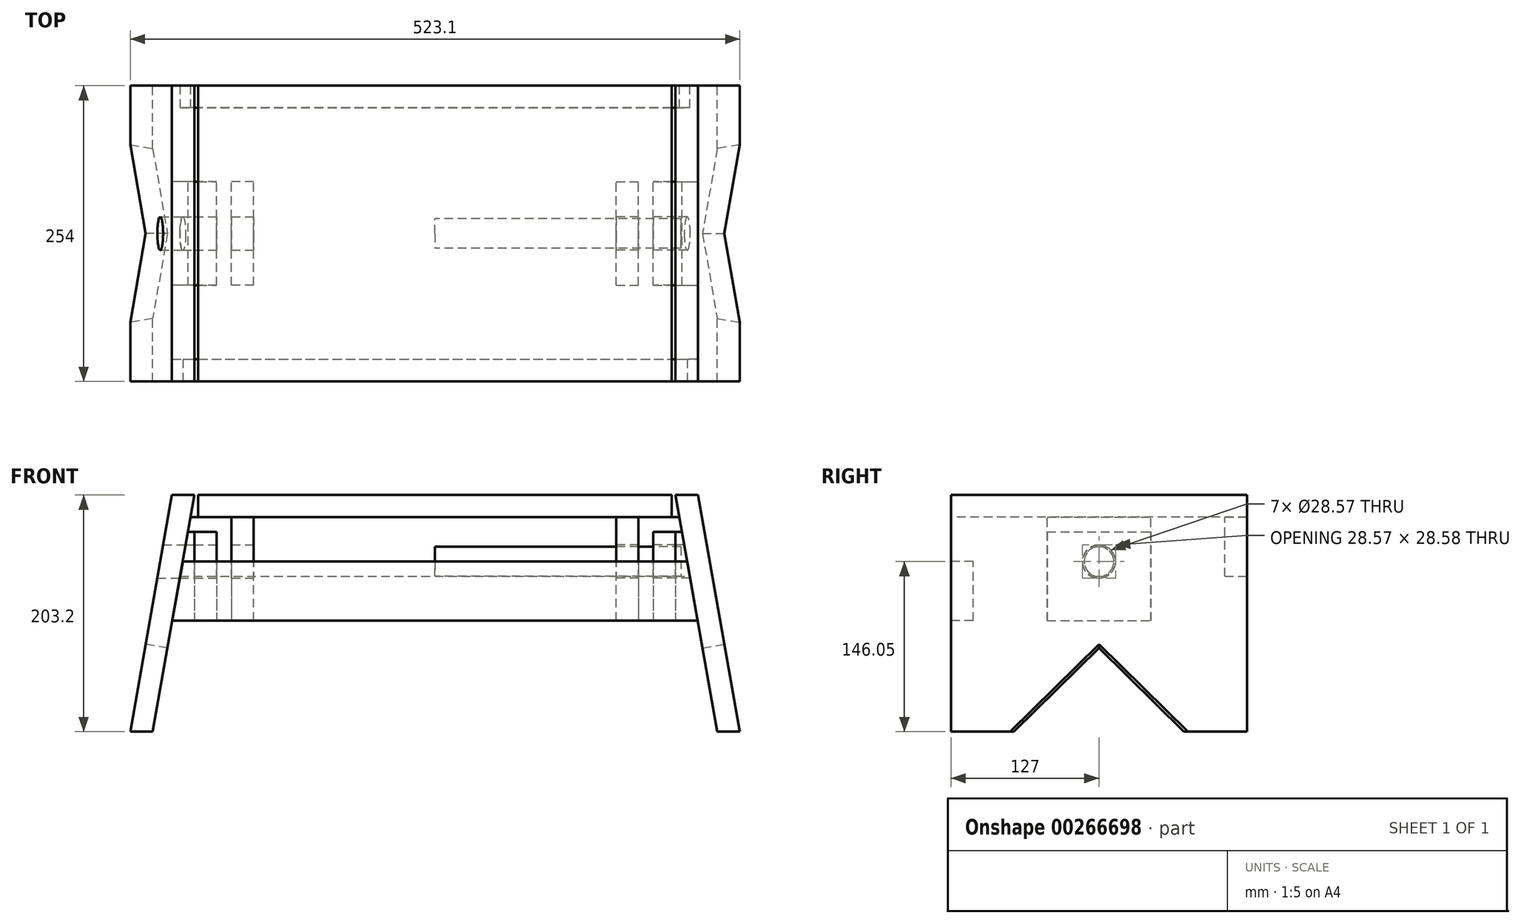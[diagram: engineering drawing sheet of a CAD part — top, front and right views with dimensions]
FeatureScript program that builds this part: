
annotation { "Feature Type Name" : "Feature", "Feature Type Description" : "" }
export const myFeature = defineFeature(function(context is Context, id is Id, definition is map)
    precondition{}
    {
        {
            var Q0;
            Q0=qCreatedBy(makeId("Top.planeOp"),FACE);
            var sketch = newSketch(context, id + "F0", { "sketchPlane" : qUnion([Q0])});
            skLineSegment(sketch, "E0.bottom", {"start": v(-203.2, 127) * mm, "end": v(203.2, 127) * mm});
            skLineSegment(sketch, "E0.top", {"start": v(-203.2, -127) * mm, "end": v(203.2, -127) * mm});
            skLineSegment(sketch, "E0.left", {"start": v(-203.2, 127) * mm, "end": v(-203.2, -127) * mm});
            skLineSegment(sketch, "E0.right", {"start": v(203.2, 127) * mm, "end": v(203.2, -127) * mm});
            skPoint(sketch, "E0.middle", {"position": v(0, 0) * mm});
            skSolve(sketch);
        }
        {
            var Q0;
            Q0 = qSketchRegion(id + "F0", true);
            extrude(context, id + "F1", {"entities" : qUnion([Q0]), "depth" : 19.05 * mm});
        }
        {
            var Q0;
            Q0=qCreatedBy(makeId("Front.planeOp"),FACE);
            var sketch = newSketch(context, id + "F2", { "sketchPlane" : qUnion([Q0])});
            skLineSegment(sketch, "E1", {"start": v(225.72, 19.05) * mm, "end": v(206.38, 19.05) * mm});
            skLineSegment(sketch, "E2", {"start": v(206.38, 19.05) * mm, "end": v(242.2, -184.15) * mm});
            skLineSegment(sketch, "E3", {"start": v(242.2, -184.15) * mm, "end": v(261.55, -184.15) * mm});
            skLineSegment(sketch, "E4", {"start": v(261.55, -184.15) * mm, "end": v(225.72, 19.05) * mm});
            skSolve(sketch);
        }
        {
            var Q0;
            Q0 = qSketchRegion(id + "F2", true);
            var Q1;
            Q1=makeQuery(id+"F1.opExtrude","SWEPT_FACE",FACE,{"disambiguationData":[OSD([sQuery(id+"F0.wireOp",EDGE,"E0.top")])]});
            var Q2;
            Q2=makeQuery(id+"F1.opExtrude","SWEPT_FACE",FACE,{"disambiguationData":[OSD([sQuery(id+"F0.wireOp",EDGE,"E0.bottom")])]});
            extrude(context, id + "F3", {"entities" : qUnion([Q0]), "endBound" : BoundingType.UP_TO_SURFACE, "endBoundEntityFace" : qUnion([Q1]), "depth" : 25.4 * mm, "hasSecondDirection" : true, "secondDirectionBound" : SecondDirectionBoundingType.UP_TO_SURFACE, "secondDirectionOppositeDirection" : true, "secondDirectionBoundEntityFace" : qUnion([Q2]), "secondDirectionDepth" : 25.4 * mm});
        }
        {
            var Q0;
            Q0=makeQuery(id+"F3.opExtrude","SWEPT_FACE",FACE,{"disambiguationData":[OSD([sQuery(id+"F2.wireOp",EDGE,"E4")])]});
            var sketch = newSketch(context, id + "F4", { "sketchPlane" : qUnion([Q0])});
            skLineSegment(sketch, "E5", {"start": v(-76.2, -226.77) * mm, "end": v(0, -150.57) * mm});
            skLineSegment(sketch, "E6", {"start": v(0, -150.57) * mm, "end": v(76.2, -226.77) * mm});
            skLineSegment(sketch, "E7", {"start": v(76.2, -226.77) * mm, "end": v(-76.2, -226.77) * mm});
            skSolve(sketch);
        }
        {
            var Q0;
            Q0 = qSketchRegion(id + "F4", true);
            extrude(context, id + "F5", {"entities" : qUnion([Q0]), "operationType" : NewBodyOperationType.REMOVE, "endBound" : BoundingType.UP_TO_NEXT, "oppositeDirection" : true, "depth" : 25.4 * mm});
        }
        {
            var Q0;
            Q0=makeQuery(id+"F3.opExtrude","SWEPT_BODY",BODY,{"disambiguationData":[OSD([sQuery(id+"F2.wireOp",EDGE,"E1"),sQuery(id+"F2.wireOp",EDGE,"E2"),sQuery(id+"F2.wireOp",EDGE,"E3"),sQuery(id+"F2.wireOp",EDGE,"E4")])]});
            var Q1;
            Q1=qCreatedBy(makeId("Right.planeOp"),FACE);
            mirror(context, id + "F6", {"entities" : qUnion([Q0]), "mirrorPlane" : qUnion([Q1])});
        }
        {
            var Q0;
            Q0=makeQuery(id+"F1.opExtrude","SWEPT_FACE",FACE,{"disambiguationData":[OSD([sQuery(id+"F0.wireOp",EDGE,"E0.top")])]});
            var sketch = newSketch(context, id + "F7", { "sketchPlane" : qUnion([Q0])});
            skLineSegment(sketch, "E8.0", {"start": v(-225.4, -88.9) * mm, "end": v(-216.45, -38.1) * mm});
            skLineSegment(sketch, "E9.0", {"start": v(225.4, -88.9) * mm, "end": v(216.45, -38.1) * mm});
            skLineSegment(sketch, "E10", {"start": v(-225.4, -88.9) * mm, "end": v(225.4, -88.9) * mm});
            skPoint(sketch, "E11.orphan", {"position": v(-242.2, -184.15) * mm});
            skPoint(sketch, "E12.orphan", {"position": v(242.2, -184.15) * mm});
            skLineSegment(sketch, "E13", {"start": v(-216.45, -38.1) * mm, "end": v(216.45, -38.1) * mm});
            skSolve(sketch);
        }
        {
            var Q0;
            Q0 = qSketchRegion(id + "F7", true);
            extrude(context, id + "F8", {"entities" : qUnion([Q0]), "oppositeDirection" : true, "depth" : 19.05 * mm});
        }
        {
            var Q0;
            Q0=qCreatedBy(makeId("Front.planeOp"),FACE);
            var sketch = newSketch(context, id + "F9", { "sketchPlane" : qUnion([Q0])});
            skLineSegment(sketch, "E14.bottom", {"start": v(-211.04, -25.4) * mm, "end": v(211.04, -25.4) * mm});
            skLineSegment(sketch, "E14.top", {"start": v(-211.04, -50.8) * mm, "end": v(211.04, -50.8) * mm});
            skLineSegment(sketch, "E14.left", {"start": v(-211.04, -25.4) * mm, "end": v(-211.04, -50.8) * mm});
            skLineSegment(sketch, "E14.right", {"start": v(211.04, -25.4) * mm, "end": v(211.04, -50.8) * mm});
            skLineSegment(sketch, "E15", {"start": v(-211.04, -25.4) * mm, "end": v(-214.21, -25.4) * mm, "construction": true});
            skLineSegment(sketch, "E16", {"start": v(-211.04, -38.1) * mm, "end": v(211.04, -38.1) * mm});
            skLineSegment(sketch, "E17", {"start": v(-206.36, -12.7) * mm, "end": v(-206.36, -88.9) * mm});
            skLineSegment(sketch, "E18", {"start": v(-206.36, -88.9) * mm, "end": v(-225.4, -88.9) * mm});
            skLineSegment(sketch, "E19", {"start": v(-206.36, -12.7) * mm, "end": v(-211.97, -12.7) * mm});
            skLineSegment(sketch, "E20", {"start": v(-211.97, -12.7) * mm, "end": v(-225.4, -88.9) * mm});
            skLineSegment(sketch, "E21", {"start": v(-174.6, 0) * mm, "end": v(-174.6, -88.9) * mm});
            skLineSegment(sketch, "E22", {"start": v(-174.6, -88.9) * mm, "end": v(-155.56, -88.9) * mm});
            skLineSegment(sketch, "E23", {"start": v(-155.56, -88.9) * mm, "end": v(-155.56, 0) * mm});
            skLineSegment(sketch, "E24", {"start": v(-155.56, 0) * mm, "end": v(-174.6, 0) * mm});
            skLineSegment(sketch, "E25", {"start": v(-174.6, -23.81) * mm, "end": v(-155.56, -23.81) * mm});
            skLineSegment(sketch, "E26", {"start": v(-174.6, -52.39) * mm, "end": v(-155.56, -52.39) * mm});
            skLineSegment(sketch, "E27", {"start": v(-206.36, -12.7) * mm, "end": v(-187.3, -12.7) * mm});
            skLineSegment(sketch, "E28", {"start": v(-187.3, -12.7) * mm, "end": v(-187.3, -88.9) * mm});
            skLineSegment(sketch, "E29", {"start": v(-187.3, -88.9) * mm, "end": v(-206.36, -88.9) * mm});
            skSolve(sketch);
        }
        {
            var Q0;
            Q0=qCreatedBy(makeId("Right.planeOp"),FACE);
            var sketch = newSketch(context, id + "F10", { "sketchPlane" : qUnion([Q0])});
            skCircle(sketch, "E30", {"center": v(0, -38.1) * mm, "radius": 12.7 * mm});
            skLineSegment(sketch, "E31", {"start": v(0, -38.1) * mm, "end": v(-17.15, 16.42) * mm, "construction": true});
            skLineSegment(sketch, "E32", {"start": v(-138.3, -21.68) * mm, "end": v(104, 54.52) * mm, "construction": true});
            skLineSegment(sketch, "E33", {"start": v(0, -38.1) * mm, "end": v(0, 19.05) * mm, "construction": true});
            skLineSegment(sketch, "E34", {"start": v(-138.3, -21.68) * mm, "end": v(-132.58, -39.85) * mm, "construction": true});
            skLineSegment(sketch, "E35", {"start": v(-132.58, -39.85) * mm, "end": v(109.72, 36.35) * mm, "construction": true});
            skLineSegment(sketch, "E36", {"start": v(109.72, 36.35) * mm, "end": v(104, 54.52) * mm, "construction": true});
            skCircle(sketch, "E37", {"center": v(0, -38.1) * mm, "radius": 14.29 * mm});
            skPoint(sketch, "E38.0", {"position": v(0, -25.4) * mm});
            skPoint(sketch, "E39.0", {"position": v(0, -23.81) * mm});
            skSolve(sketch);
        }
        {
            var Q0;
            {var subQ0=sQuery(id+"F9.wireOp",EDGE,"E19");Q0=makeQuery(id+"F9.imprint","IMPRINT",FACE,{"disambiguationData":[TD([[makeQuery(id+"F9.imprint","IMPRINT",EDGE,{"derivedFrom":subQ0}),1.0]])]});}
            var Q1;
            {var subQ0=sQuery(id+"F9.wireOp",EDGE,"E18");Q1=makeQuery(id+"F9.imprint","IMPRINT",FACE,{"disambiguationData":[TD([[makeQuery(id+"F9.imprint","IMPRINT",EDGE,{"derivedFrom":subQ0}),-1.0]])]});}
            var Q2;
            {var subQ5=sQuery(id+"F9.wireOp",EDGE,"QS01VHn4-kFqK-0E2x-3ZNE-qvUShlXBOCAW");Q2=makeQuery(id+"F9.imprint","IMPRINT",FACE,{"disambiguationData":[TD([[makeQuery(id+"F9.imprint","IMPRINT",EDGE,{"derivedFrom":subQ5}),1.0]])]});}
            var Q3;
            {var subQ0=sQuery(id+"F9.wireOp",EDGE,"E14.left");var subQ1=sQuery(id+"F9.wireOp",EDGE,"E14.bottom");var subQ2=makeQuery(id+"F9.imprint","INTERSECT",VERTEX,{"derivedFrom":[subQ1,subQ0]});Q3=makeQuery(id+"F9.imprint","IMPRINT",FACE,{"disambiguationData":[TD([[makeQuery(id+"F9.imprint","IMPRINT",EDGE,{"disambiguationData":[TD([[subQ2,-1.0]])],"derivedFrom":subQ1}),-1.0]])]});}
            var Q4;
            {var subQ0=sQuery(id+"F9.wireOp",EDGE,"E14.left");var subQ1=sQuery(id+"F9.wireOp",EDGE,"E14.top");var subQ2=makeQuery(id+"F9.imprint","INTERSECT",VERTEX,{"derivedFrom":[subQ1,subQ0]});Q4=makeQuery(id+"F9.imprint","IMPRINT",FACE,{"disambiguationData":[TD([[makeQuery(id+"F9.imprint","IMPRINT",EDGE,{"disambiguationData":[TD([[subQ2,-1.0]])],"derivedFrom":subQ1}),1.0]])]});}
            var Q5;
            Q5=sQuery(id+"F9.wireOp",EDGE,"E17");
            var Q6;
            Q6=sQuery(id+"F9.wireOp",EDGE,"E18");
            var Q7;
            Q7=sQuery(id+"F9.wireOp",EDGE,"E20");
            var Q8;
            Q8=sQuery(id+"F9.wireOp",EDGE,"E19");
            extrude(context, id + "F11", {"entities" : qUnion([Q0, Q1, Q2, Q3, Q4]), "surfaceEntities" : qUnion([Q5, Q6, Q7, Q8]), "endBound" : BoundingType.SYMMETRIC, "depth" : 88.9 * mm});
        }
        {
            var Q0;
            Q0=makeQuery(id+"F10.imprint","IMPRINT",FACE,{"disambiguationData":[TD([[makeQuery(id+"F10.imprint","IMPRINT",EDGE,{"derivedFrom":sQuery(id+"F10.wireOp",EDGE,"E30")}),-1.0]])]});
            var Q1;
            Q1=makeQuery(id+"F10.imprint","IMPRINT",FACE,{"disambiguationData":[TD([[makeQuery(id+"F10.imprint","IMPRINT",EDGE,{"derivedFrom":sQuery(id+"F10.wireOp",EDGE,"E30")}),1.0]])]});
            extrude(context, id + "F12", {"entities" : qUnion([Q0, Q1]), "operationType" : NewBodyOperationType.REMOVE, "endBound" : BoundingType.THROUGH_ALL, "oppositeDirection" : true, "depth" : 25.4 * mm});
        }
        {
            var Q0;
            {var subQ0=sQuery(id+"F9.wireOp",EDGE,"E14.right");var subQ1=sQuery(id+"F9.wireOp",EDGE,"E14.top");var subQ2=makeQuery(id+"F9.imprint","INTERSECT",VERTEX,{"derivedFrom":[subQ1,subQ0]});Q0=makeQuery(id+"F9.imprint","IMPRINT",FACE,{"disambiguationData":[TD([[makeQuery(id+"F9.imprint","IMPRINT",EDGE,{"disambiguationData":[TD([[subQ2,1.0]])],"derivedFrom":subQ1}),1.0]])]});}
            var Q1;
            {var subQ0=sQuery(id+"F9.wireOp",EDGE,"E14.left");var subQ1=sQuery(id+"F9.wireOp",EDGE,"E14.top");var subQ2=makeQuery(id+"F9.imprint","INTERSECT",VERTEX,{"derivedFrom":[subQ1,subQ0]});Q1=makeQuery(id+"F9.imprint","IMPRINT",FACE,{"disambiguationData":[TD([[makeQuery(id+"F9.imprint","IMPRINT",EDGE,{"disambiguationData":[TD([[subQ2,-1.0]])],"derivedFrom":subQ1}),1.0]])]});}
            var Q2;
            {var subQ0=sQuery(id+"F9.wireOp",EDGE,"E21");var subQ1=sQuery(id+"F9.wireOp",EDGE,"E14.top");var subQ2=makeQuery(id+"F9.imprint","INTERSECT",VERTEX,{"derivedFrom":[subQ1,subQ0]});Q2=makeQuery(id+"F9.imprint","IMPRINT",FACE,{"disambiguationData":[TD([[makeQuery(id+"F9.imprint","IMPRINT",EDGE,{"disambiguationData":[TD([[subQ2,-1.0]])],"derivedFrom":subQ1}),1.0]])]});}
            var Q3;
            {var subQ0=sQuery(id+"F9.wireOp",EDGE,"E17");var subQ1=sQuery(id+"F9.wireOp",EDGE,"E14.top");var subQ2=makeQuery(id+"F9.imprint","INTERSECT",VERTEX,{"derivedFrom":[subQ1,subQ0]});Q3=makeQuery(id+"F9.imprint","IMPRINT",FACE,{"disambiguationData":[TD([[makeQuery(id+"F9.imprint","IMPRINT",EDGE,{"disambiguationData":[TD([[subQ2,-1.0]])],"derivedFrom":subQ1}),1.0]])]});}
            var Q4;
            {var subQ0=sQuery(id+"F9.wireOp",EDGE,"E28");var subQ1=sQuery(id+"F9.wireOp",EDGE,"E14.top");var subQ2=makeQuery(id+"F9.imprint","INTERSECT",VERTEX,{"derivedFrom":[subQ1,subQ0]});Q4=makeQuery(id+"F9.imprint","IMPRINT",FACE,{"disambiguationData":[TD([[makeQuery(id+"F9.imprint","IMPRINT",EDGE,{"disambiguationData":[TD([[subQ2,-1.0]])],"derivedFrom":subQ1}),1.0]])]});}
            var Q5;
            Q5=sQuery(id+"F9.wireOp",EDGE,"E16");
            revolve(context, id + "F13", {"entities" : qUnion([Q0, Q1, Q2, Q3, Q4]), "axis" : qUnion([Q5]), "revolveType" : RevolveType.FULL});
        }
        {
            var Q0;
            Q0=makeQuery(id+"F11.opExtrude","SWEPT_BODY",BODY,{"disambiguationData":[OSD([sQuery(id+"F9.wireOp",EDGE,"E17"),sQuery(id+"F9.wireOp",EDGE,"E18"),sQuery(id+"F9.wireOp",EDGE,"E19"),sQuery(id+"F9.wireOp",EDGE,"E20")])]});
            var Q1;
            Q1=qCreatedBy(makeId("Right.planeOp"),FACE);
            mirror(context, id + "F14", {"entities" : qUnion([Q0]), "mirrorPlane" : qUnion([Q1])});
        }
        {
            var Q0;
            {var subQ0=sQuery(id+"F9.wireOp",EDGE,"E22");Q0=makeQuery(id+"F9.imprint","IMPRINT",FACE,{"disambiguationData":[TD([[makeQuery(id+"F9.imprint","IMPRINT",EDGE,{"derivedFrom":subQ0}),1.0]])]});}
            var Q1;
            {var subQ0=sQuery(id+"F9.wireOp",EDGE,"E24");Q1=makeQuery(id+"F9.imprint","IMPRINT",FACE,{"disambiguationData":[TD([[makeQuery(id+"F9.imprint","IMPRINT",EDGE,{"derivedFrom":subQ0}),1.0]])]});}
            var Q2;
            {var subQ5=sQuery(id+"F9.wireOp",EDGE,"E25");Q2=makeQuery(id+"F9.imprint","IMPRINT",FACE,{"disambiguationData":[TD([[makeQuery(id+"F9.imprint","IMPRINT",EDGE,{"derivedFrom":subQ5}),-1.0]])]});}
            var Q3;
            {var subQ0=sQuery(id+"F9.wireOp",EDGE,"E21");var subQ1=sQuery(id+"F9.wireOp",EDGE,"E14.bottom");var subQ2=makeQuery(id+"F9.imprint","INTERSECT",VERTEX,{"derivedFrom":[subQ1,subQ0]});Q3=makeQuery(id+"F9.imprint","IMPRINT",FACE,{"disambiguationData":[TD([[makeQuery(id+"F9.imprint","IMPRINT",EDGE,{"disambiguationData":[TD([[subQ2,-1.0]])],"derivedFrom":subQ1}),-1.0]])]});}
            var Q4;
            {var subQ5=sQuery(id+"F9.wireOp",EDGE,"E26");Q4=makeQuery(id+"F9.imprint","IMPRINT",FACE,{"disambiguationData":[TD([[makeQuery(id+"F9.imprint","IMPRINT",EDGE,{"derivedFrom":subQ5}),1.0]])]});}
            var Q5;
            {var subQ0=sQuery(id+"F9.wireOp",EDGE,"E21");var subQ1=sQuery(id+"F9.wireOp",EDGE,"E14.top");var subQ2=makeQuery(id+"F9.imprint","INTERSECT",VERTEX,{"derivedFrom":[subQ1,subQ0]});Q5=makeQuery(id+"F9.imprint","IMPRINT",FACE,{"disambiguationData":[TD([[makeQuery(id+"F9.imprint","IMPRINT",EDGE,{"disambiguationData":[TD([[subQ2,-1.0]])],"derivedFrom":subQ1}),1.0]])]});}
            extrude(context, id + "F15", {"entities" : qUnion([Q0, Q1, Q2, Q3, Q4, Q5]), "endBound" : BoundingType.SYMMETRIC, "depth" : 88.9 * mm});
        }
        {
            var Q0;
            Q0=makeQuery(id+"F10.imprint","IMPRINT",FACE,{"disambiguationData":[TD([[makeQuery(id+"F10.imprint","IMPRINT",EDGE,{"derivedFrom":sQuery(id+"F10.wireOp",EDGE,"E30")}),1.0]])]});
            var Q1;
            Q1=makeQuery(id+"F10.imprint","IMPRINT",FACE,{"disambiguationData":[TD([[makeQuery(id+"F10.imprint","IMPRINT",EDGE,{"derivedFrom":sQuery(id+"F10.wireOp",EDGE,"E30")}),-1.0]])]});
            extrude(context, id + "F16", {"entities" : qUnion([Q0, Q1]), "operationType" : NewBodyOperationType.REMOVE, "endBound" : BoundingType.THROUGH_ALL, "oppositeDirection" : true, "depth" : 25.4 * mm});
        }
        {
            var Q0;
            Q0=makeQuery(id+"F15.opExtrude","SWEPT_BODY",BODY,{"disambiguationData":[OSD([sQuery(id+"F9.wireOp",EDGE,"E21"),sQuery(id+"F9.wireOp",EDGE,"E22"),sQuery(id+"F9.wireOp",EDGE,"E23"),sQuery(id+"F9.wireOp",EDGE,"E24")])]});
            var Q1;
            Q1=qCreatedBy(makeId("Right.planeOp"),FACE);
            mirror(context, id + "F17", {"entities" : qUnion([Q0]), "mirrorPlane" : qUnion([Q1])});
        }
        {
            var Q0;
            Q0=makeQuery(id+"F1.opExtrude","SWEPT_FACE",FACE,{"disambiguationData":[OSD([sQuery(id+"F0.wireOp",EDGE,"E0.bottom")])]});
            var sketch = newSketch(context, id + "F18", { "sketchPlane" : qUnion([Q0])});
            skLineSegment(sketch, "E40", {"start": v(-209.73, 0) * mm, "end": v(209.73, 0) * mm});
            skLineSegment(sketch, "E41", {"start": v(209.73, 0) * mm, "end": v(218.7, -50.8) * mm});
            skLineSegment(sketch, "E42", {"start": v(218.7, -50.8) * mm, "end": v(-218.7, -50.8) * mm});
            skLineSegment(sketch, "E43", {"start": v(-218.7, -50.8) * mm, "end": v(-209.73, 0) * mm});
            skSolve(sketch);
        }
        {
            var Q0;
            Q0 = qSketchRegion(id + "F18", true);
            extrude(context, id + "F19", {"entities" : qUnion([Q0]), "oppositeDirection" : true, "depth" : 19.05 * mm});
        }
        {
            var Q0;
            {var subQ5=sQuery(id+"F9.wireOp",EDGE,"E27");Q0=makeQuery(id+"F9.imprint","IMPRINT",FACE,{"disambiguationData":[TD([[makeQuery(id+"F9.imprint","IMPRINT",EDGE,{"derivedFrom":subQ5}),-1.0]])]});}
            var Q1;
            {var subQ0=sQuery(id+"F9.wireOp",EDGE,"E28");var subQ1=sQuery(id+"F9.wireOp",EDGE,"E14.bottom");var subQ2=makeQuery(id+"F9.imprint","INTERSECT",VERTEX,{"derivedFrom":[subQ1,subQ0]});Q1=makeQuery(id+"F9.imprint","IMPRINT",FACE,{"disambiguationData":[TD([[makeQuery(id+"F9.imprint","IMPRINT",EDGE,{"disambiguationData":[TD([[subQ2,1.0]])],"derivedFrom":subQ1}),-1.0]])]});}
            var Q2;
            {var subQ0=sQuery(id+"F9.wireOp",EDGE,"E28");var subQ1=sQuery(id+"F9.wireOp",EDGE,"E14.top");var subQ2=makeQuery(id+"F9.imprint","INTERSECT",VERTEX,{"derivedFrom":[subQ1,subQ0]});Q2=makeQuery(id+"F9.imprint","IMPRINT",FACE,{"disambiguationData":[TD([[makeQuery(id+"F9.imprint","IMPRINT",EDGE,{"disambiguationData":[TD([[subQ2,1.0]])],"derivedFrom":subQ1}),1.0]])]});}
            var Q3;
            {var subQ5=sQuery(id+"F9.wireOp",EDGE,"E29");Q3=makeQuery(id+"F9.imprint","IMPRINT",FACE,{"disambiguationData":[TD([[makeQuery(id+"F9.imprint","IMPRINT",EDGE,{"derivedFrom":subQ5}),-1.0]])]});}
            extrude(context, id + "F20", {"entities" : qUnion([Q0, Q1, Q2, Q3]), "endBound" : BoundingType.SYMMETRIC, "depth" : 88.9 * mm});
        }
        {
            var Q0;
            Q0=makeQuery(id+"F10.imprint","IMPRINT",FACE,{"disambiguationData":[TD([[makeQuery(id+"F10.imprint","IMPRINT",EDGE,{"derivedFrom":sQuery(id+"F10.wireOp",EDGE,"E30")}),-1.0]])]});
            var Q1;
            Q1=makeQuery(id+"F10.imprint","IMPRINT",FACE,{"disambiguationData":[TD([[makeQuery(id+"F10.imprint","IMPRINT",EDGE,{"derivedFrom":sQuery(id+"F10.wireOp",EDGE,"E30")}),1.0]])]});
            extrude(context, id + "F21", {"entities" : qUnion([Q0, Q1]), "operationType" : NewBodyOperationType.REMOVE, "endBound" : BoundingType.THROUGH_ALL, "oppositeDirection" : true, "depth" : 25.4 * mm});
        }
        {
            var Q0;
            Q0=makeQuery(id+"F20.opExtrude","SWEPT_BODY",BODY,{"disambiguationData":[OSD([sQuery(id+"F9.wireOp",EDGE,"E17"),sQuery(id+"F9.wireOp",EDGE,"E27"),sQuery(id+"F9.wireOp",EDGE,"E28"),sQuery(id+"F9.wireOp",EDGE,"E29")])]});
            var Q1;
            Q1=qCreatedBy(makeId("Right.planeOp"),FACE);
            mirror(context, id + "F22", {"entities" : qUnion([Q0]), "mirrorPlane" : qUnion([Q1])});
        }
    });
